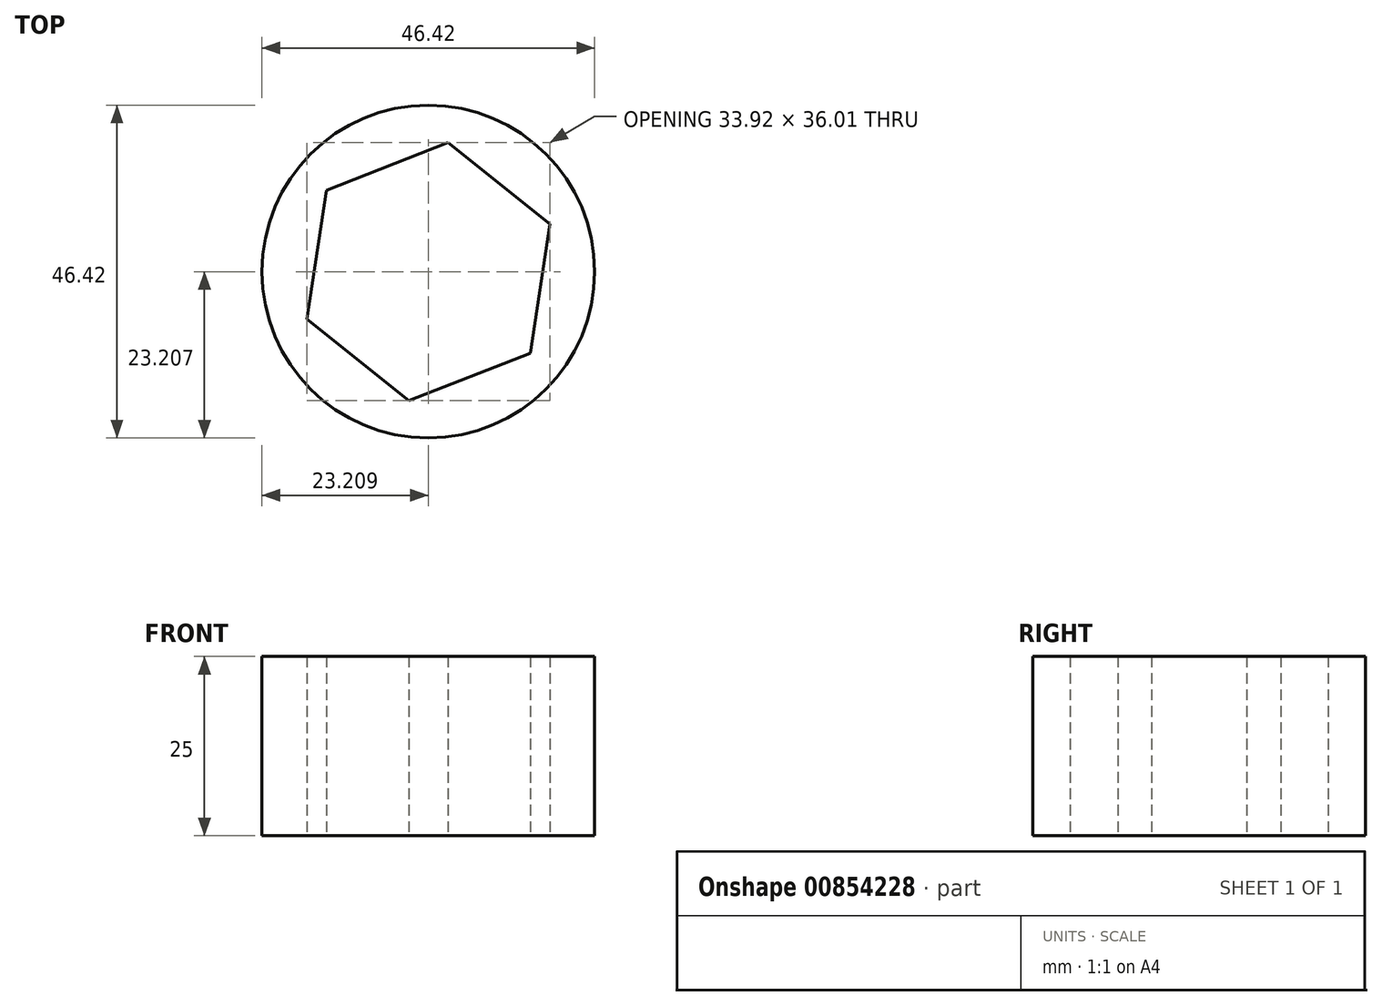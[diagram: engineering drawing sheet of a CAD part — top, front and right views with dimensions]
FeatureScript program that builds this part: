
annotation { "Feature Type Name" : "Feature", "Feature Type Description" : "" }
export const myFeature = defineFeature(function(context is Context, id is Id, definition is map)
    precondition{}
    {
        {
            var Q0;
            Q0=qCreatedBy(makeId("Top.planeOp"),FACE);
            var sketch = newSketch(context, id + "F0", { "sketchPlane" : qUnion([Q0])});
            skCircle(sketch, "E0", {"center": v(-52.18, 40.06) * mm, "radius": 18.21 * mm});
            skCircle(sketch, "E1.cCircle", {"center": v(-52.18, 40.06) * mm, "radius": 18.21 * mm, "construction": true});
            skLineSegment(sketch, "E1.0", {"start": v(-37.96, 28.69) * mm, "end": v(-54.91, 22.05) * mm});
            skLineSegment(sketch, "E1.1", {"start": v(-54.91, 22.05) * mm, "end": v(-69.14, 33.42) * mm});
            skLineSegment(sketch, "E1.2", {"start": v(-69.14, 33.42) * mm, "end": v(-66.4, 51.43) * mm});
            skLineSegment(sketch, "E1.3", {"start": v(-66.4, 51.43) * mm, "end": v(-49.45, 58.06) * mm});
            skLineSegment(sketch, "E1.4", {"start": v(-49.45, 58.06) * mm, "end": v(-35.22, 46.7) * mm});
            skLineSegment(sketch, "E1.5", {"start": v(-35.22, 46.7) * mm, "end": v(-37.96, 28.69) * mm});
            skCircle(sketch, "E2.0", {"center": v(-52.18, 40.06) * mm, "radius": 23.21 * mm});
            skLineSegment(sketch, "E3.bottom", {"start": v(-43.19, 33.62) * mm, "end": v(-61.17, 33.62) * mm});
            skLineSegment(sketch, "E3.top", {"start": v(-43.19, 46.49) * mm, "end": v(-61.17, 46.49) * mm});
            skLineSegment(sketch, "E3.left", {"start": v(-43.19, 33.62) * mm, "end": v(-43.19, 46.49) * mm});
            skLineSegment(sketch, "E3.right", {"start": v(-61.17, 33.62) * mm, "end": v(-61.17, 46.49) * mm});
            skSolve(sketch);
        }
        {
            var Q0;
            {var subQ0=sQuery(id+"F0.wireOp",EDGE,"E1.4");Q0=makeQuery(id+"F0.imprint","IMPRINT",FACE,{"disambiguationData":[TD([[makeQuery(id+"F0.imprint","IMPRINT",EDGE,{"derivedFrom":subQ0}),1.0]])]});}
            var Q1;
            {var subQ0=sQuery(id+"F0.wireOp",EDGE,"E1.3");Q1=makeQuery(id+"F0.imprint","IMPRINT",FACE,{"disambiguationData":[TD([[makeQuery(id+"F0.imprint","IMPRINT",EDGE,{"derivedFrom":subQ0}),1.0]])]});}
            var Q2;
            {var subQ0=sQuery(id+"F0.wireOp",EDGE,"E1.5");Q2=makeQuery(id+"F0.imprint","IMPRINT",FACE,{"disambiguationData":[TD([[makeQuery(id+"F0.imprint","IMPRINT",EDGE,{"derivedFrom":subQ0}),1.0]])]});}
            var Q3;
            {var subQ0=sQuery(id+"F0.wireOp",EDGE,"E1.0");Q3=makeQuery(id+"F0.imprint","IMPRINT",FACE,{"disambiguationData":[TD([[makeQuery(id+"F0.imprint","IMPRINT",EDGE,{"derivedFrom":subQ0}),1.0]])]});}
            var Q4;
            {var subQ0=sQuery(id+"F0.wireOp",EDGE,"E1.2");Q4=makeQuery(id+"F0.imprint","IMPRINT",FACE,{"disambiguationData":[TD([[makeQuery(id+"F0.imprint","IMPRINT",EDGE,{"derivedFrom":subQ0}),1.0]])]});}
            var Q5;
            {var subQ0=sQuery(id+"F0.wireOp",EDGE,"E1.1");Q5=makeQuery(id+"F0.imprint","IMPRINT",FACE,{"disambiguationData":[TD([[makeQuery(id+"F0.imprint","IMPRINT",EDGE,{"derivedFrom":subQ0}),1.0]])]});}
            var Q6;
            Q6=makeQuery(id+"F0.imprint","IMPRINT",FACE,{"disambiguationData":[TD([[makeQuery(id+"F0.imprint","IMPRINT",EDGE,{"derivedFrom":sQuery(id+"F0.wireOp",EDGE,"E2.0")}),1.0]])]});
            extrude(context, id + "F1", {"entities" : qUnion([Q0, Q1, Q2, Q3, Q4, Q5, Q6]), "depth" : 25 * mm, "offsetDistance" : 25 * mm});
        }
    });
